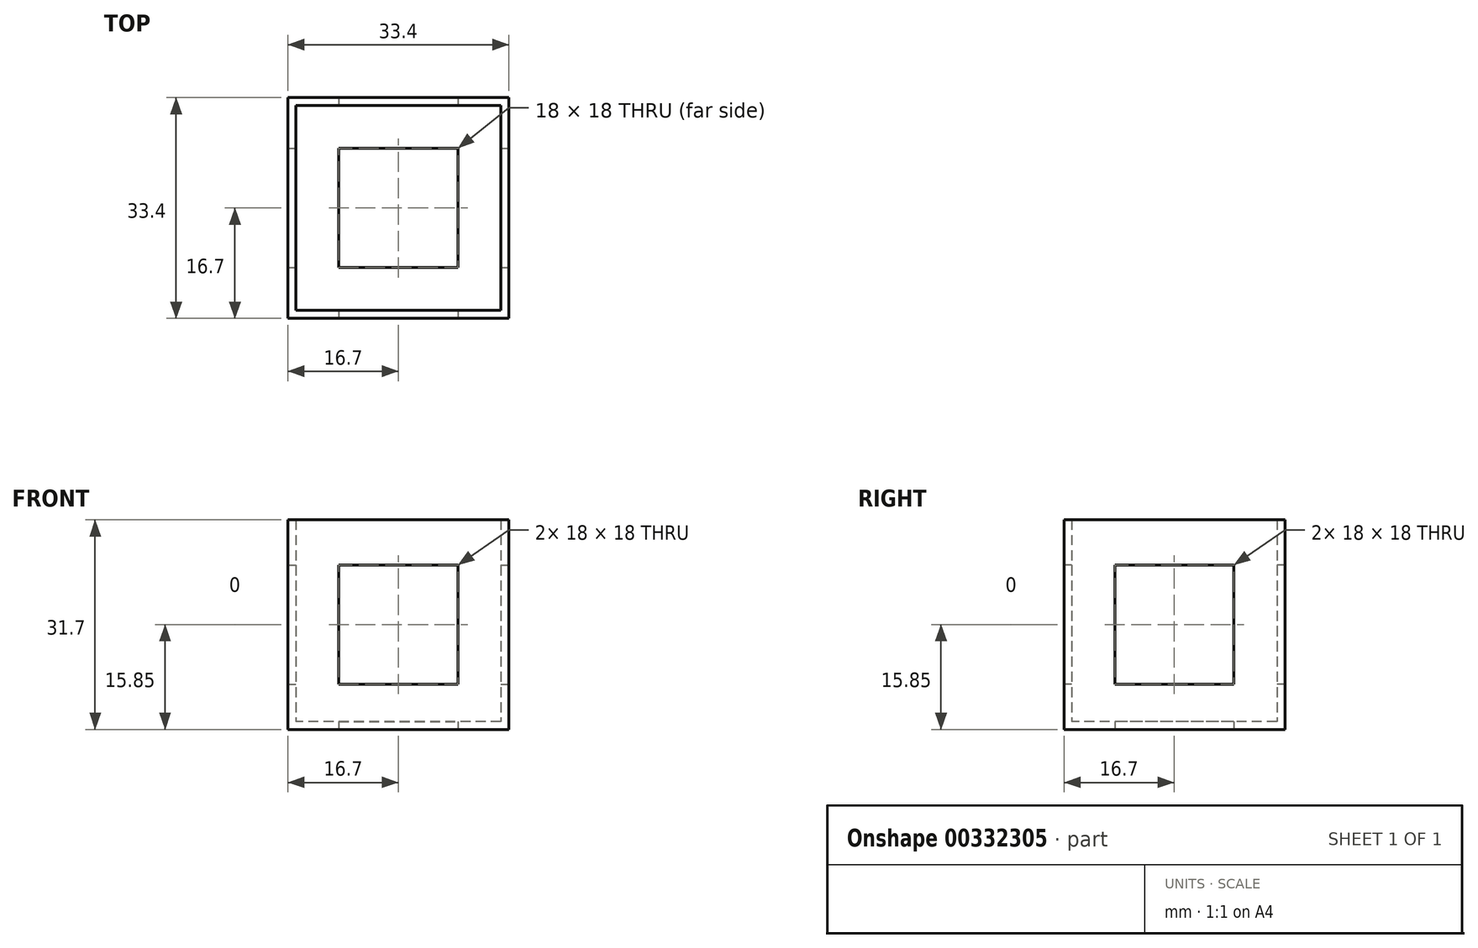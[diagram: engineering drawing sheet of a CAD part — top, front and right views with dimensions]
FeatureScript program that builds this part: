
annotation { "Feature Type Name" : "Feature", "Feature Type Description" : "" }
export const myFeature = defineFeature(function(context is Context, id is Id, definition is map)
    precondition{}
    {
        {
            var Q0;
            Q0=qCreatedBy(makeId("Top.planeOp"),FACE);
            var sketch = newSketch(context, id + "F0", { "sketchPlane" : qUnion([Q0])});
            skLineSegment(sketch, "E0.bottom", {"start": v(15.5, 15.5) * mm, "end": v(-15.5, 15.5) * mm});
            skLineSegment(sketch, "E0.top", {"start": v(15.5, -15.5) * mm, "end": v(-15.5, -15.5) * mm});
            skLineSegment(sketch, "E0.left", {"start": v(15.5, 15.5) * mm, "end": v(15.5, -15.5) * mm});
            skLineSegment(sketch, "E0.right", {"start": v(-15.5, 15.5) * mm, "end": v(-15.5, -15.5) * mm});
            skPoint(sketch, "E0.middle", {"position": v(0, 0) * mm});
            skLineSegment(sketch, "E1.0", {"start": v(16.7, 16.7) * mm, "end": v(-16.7, 16.7) * mm});
            skLineSegment(sketch, "E1.1", {"start": v(16.7, 16.7) * mm, "end": v(16.7, -16.7) * mm});
            skLineSegment(sketch, "E1.2", {"start": v(16.7, -16.7) * mm, "end": v(-16.7, -16.7) * mm});
            skLineSegment(sketch, "E1.3", {"start": v(-16.7, 16.7) * mm, "end": v(-16.7, -16.7) * mm});
            skSolve(sketch);
        }
        {
            var Q0;
            Q0=makeQuery(id+"F0.imprint","IMPRINT",FACE,{"disambiguationData":[TD([[makeQuery(id+"F0.imprint","IMPRINT",EDGE,{"derivedFrom":sQuery(id+"F0.wireOp",EDGE,"E0.bottom")}),-1.0]])]});
            extrude(context, id + "F1", {"entities" : qUnion([Q0]), "depth" : 31.7 * mm});
        }
        {
            var Q0;
            Q0=makeQuery(id+"F0.imprint","IMPRINT",FACE,{"disambiguationData":[TD([[makeQuery(id+"F0.imprint","IMPRINT",EDGE,{"derivedFrom":sQuery(id+"F0.wireOp",EDGE,"E0.bottom")}),1.0]])]});
            extrude(context, id + "F2", {"entities" : qUnion([Q0]), "operationType" : NewBodyOperationType.ADD, "depth" : 1.2 * mm});
        }
        {
            var Q0;
            Q0=makeQuery(id+"F1.opExtrude","SWEPT_FACE",FACE,{"disambiguationData":[OSD([sQuery(id+"F0.wireOp",EDGE,"E1.2")])]});
            var sketch = newSketch(context, id + "F3", { "sketchPlane" : qUnion([Q0])});
            skLineSegment(sketch, "E2.bottom", {"start": v(9, 24.85) * mm, "end": v(-9, 24.85) * mm});
            skLineSegment(sketch, "E2.top", {"start": v(9, 6.85) * mm, "end": v(-9, 6.85) * mm});
            skLineSegment(sketch, "E2.left", {"start": v(9, 24.85) * mm, "end": v(9, 6.85) * mm});
            skLineSegment(sketch, "E2.right", {"start": v(-9, 24.85) * mm, "end": v(-9, 6.85) * mm});
            skPoint(sketch, "E2.middle", {"position": v(0, 15.85) * mm});
            skPoint(sketch, "E2.middle.positionSnap0", {"position": v(-16.7, 15.85) * mm});
            skPoint(sketch, "E2.centerSnap0", {"position": v(-16.7, 15.85) * mm});
            skSolve(sketch);
        }
        {
            var Q0;
            Q0=makeQuery(id+"F3.imprint","IMPRINT",FACE,{"disambiguationData":[TD([[makeQuery(id+"F3.imprint","IMPRINT",EDGE,{"derivedFrom":sQuery(id+"F3.wireOp",EDGE,"E2.bottom")}),1.0]])]});
            extrude(context, id + "F4", {"entities" : qUnion([Q0]), "operationType" : NewBodyOperationType.REMOVE, "endBound" : BoundingType.THROUGH_ALL, "oppositeDirection" : true, "depth" : 25 * mm});
        }
        {
            var Q0;
            Q0=makeQuery(id+"F1.opExtrude","SWEPT_FACE",FACE,{"disambiguationData":[OSD([sQuery(id+"F0.wireOp",EDGE,"E1.1")])]});
            var sketch = newSketch(context, id + "F5", { "sketchPlane" : qUnion([Q0])});
            skLineSegment(sketch, "E3.bottom", {"start": v(9, 24.85) * mm, "end": v(-9, 24.85) * mm});
            skLineSegment(sketch, "E3.top", {"start": v(9, 6.85) * mm, "end": v(-9, 6.85) * mm});
            skLineSegment(sketch, "E3.left", {"start": v(9, 24.85) * mm, "end": v(9, 6.85) * mm});
            skLineSegment(sketch, "E3.right", {"start": v(-9, 24.85) * mm, "end": v(-9, 6.85) * mm});
            skPoint(sketch, "E3.middle", {"position": v(0, 15.85) * mm});
            skPoint(sketch, "E3.middle.positionSnap0", {"position": v(-16.7, 15.85) * mm});
            skPoint(sketch, "E3.centerSnap0", {"position": v(-16.7, 15.85) * mm});
            skSolve(sketch);
        }
        {
            var Q0;
            Q0=makeQuery(id+"F5.imprint","IMPRINT",FACE,{"disambiguationData":[TD([[makeQuery(id+"F5.imprint","IMPRINT",EDGE,{"derivedFrom":sQuery(id+"F5.wireOp",EDGE,"E3.bottom")}),1.0]])]});
            extrude(context, id + "F6", {"entities" : qUnion([Q0]), "operationType" : NewBodyOperationType.REMOVE, "endBound" : BoundingType.THROUGH_ALL, "oppositeDirection" : true, "depth" : 25 * mm});
        }
        {
            var Q0;
            Q0=makeQuery(id+"F0.imprint","IMPRINT",FACE,{"disambiguationData":[TD([[makeQuery(id+"F0.imprint","IMPRINT",EDGE,{"derivedFrom":sQuery(id+"F0.wireOp",EDGE,"E0.bottom")}),1.0]])]});
            var sketch = newSketch(context, id + "F7", { "sketchPlane" : qUnion([Q0])});
            skLineSegment(sketch, "E4.bottom", {"start": v(9, -9) * mm, "end": v(-9, -9) * mm});
            skLineSegment(sketch, "E4.top", {"start": v(9, 9) * mm, "end": v(-9, 9) * mm});
            skLineSegment(sketch, "E4.left", {"start": v(9, -9) * mm, "end": v(9, 9) * mm});
            skLineSegment(sketch, "E4.right", {"start": v(-9, -9) * mm, "end": v(-9, 9) * mm});
            skPoint(sketch, "E4.middle", {"position": v(0, 0) * mm});
            skSolve(sketch);
        }
        {
            var Q0;
            Q0=makeQuery(id+"F7.imprint","IMPRINT",FACE,{"disambiguationData":[TD([[makeQuery(id+"F7.imprint","IMPRINT",EDGE,{"derivedFrom":sQuery(id+"F7.wireOp",EDGE,"E4.bottom")}),-1.0]])]});
            extrude(context, id + "F8", {"entities" : qUnion([Q0]), "operationType" : NewBodyOperationType.REMOVE, "endBound" : BoundingType.THROUGH_ALL, "depth" : 25 * mm});
        }
    });
